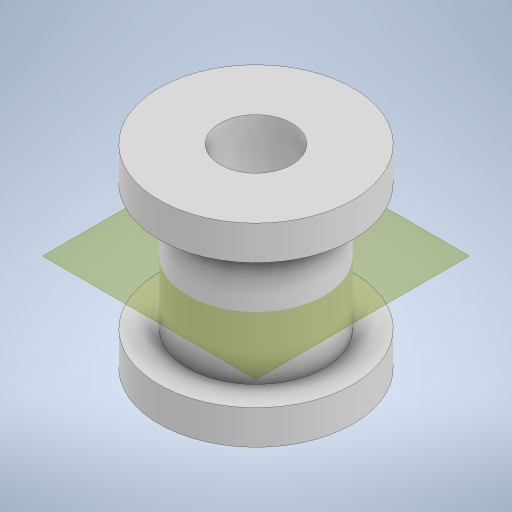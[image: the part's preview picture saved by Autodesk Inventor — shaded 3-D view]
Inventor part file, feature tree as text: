
AUTODESK INVENTOR PART (.ipt)
format: ipt  version: 2023 (Build 270158000, 158)  size: 250,368 bytes
history: native  units: mm
features: extrude x2, plane x2, sketch x2, mirror x1
ambient origin geometry x8: Origin, YZ Plane, XZ Plane, XY Plane, X Axis, Y Axis, Z Axis, Center Point
bodies: Solid1 (feature_tree)
feature tree (7):
  extrude  "Extrusion1"  Depth=12.0mm
  extrude  "Extrusion2"  Depth=17.0mm
  plane  "Work Plane1"
  mirror  "Mirror1"
  sketch  "Sketch1"  dims[d0=6.3mm d2=12.0mm]
  sketch  "Sketch2"  dims[d3=14.0mm d4=0.0mm d5=17.0mm d6=3.0mm d7=0.0mm]
  plane  "Work Plane2"
